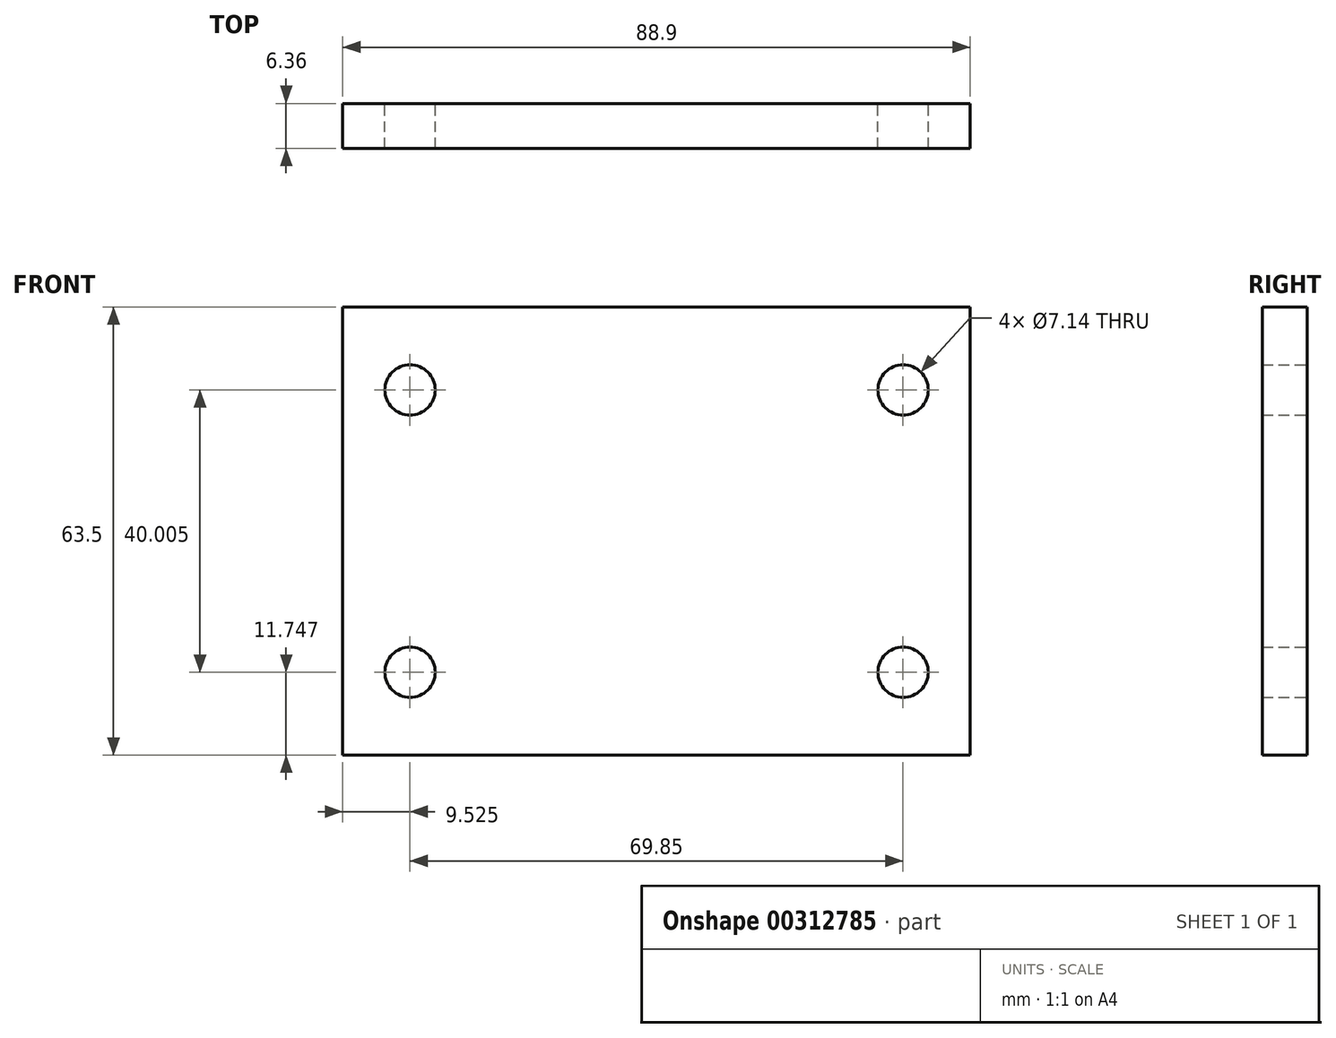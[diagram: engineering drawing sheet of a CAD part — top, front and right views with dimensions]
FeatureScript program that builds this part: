
annotation { "Feature Type Name" : "Feature", "Feature Type Description" : "" }
export const myFeature = defineFeature(function(context is Context, id is Id, definition is map)
    precondition{}
    {
        {
            var Q0;
            Q0=qCreatedBy(makeId("Front.planeOp"),FACE);
            var sketch = newSketch(context, id + "F0", { "sketchPlane" : qUnion([Q0])});
            skLineSegment(sketch, "E0.bottom", {"start": v(-44.45, 31.75) * mm, "end": v(44.45, 31.75) * mm});
            skLineSegment(sketch, "E0.top", {"start": v(-44.45, -31.75) * mm, "end": v(44.45, -31.75) * mm});
            skLineSegment(sketch, "E0.left", {"start": v(-44.45, 31.75) * mm, "end": v(-44.45, -31.75) * mm});
            skLineSegment(sketch, "E0.right", {"start": v(44.45, 31.75) * mm, "end": v(44.45, -31.75) * mm});
            skPoint(sketch, "E0.middle", {"position": v(0, 0) * mm});
            skCircle(sketch, "E1", {"center": v(-34.93, 20) * mm, "radius": 3.57 * mm});
            skCircle(sketch, "E2", {"center": v(-34.93, -20) * mm, "radius": 3.57 * mm});
            skCircle(sketch, "E3", {"center": v(34.93, -20) * mm, "radius": 3.57 * mm});
            skCircle(sketch, "E4", {"center": v(34.93, 20) * mm, "radius": 3.57 * mm});
            skLineSegment(sketch, "E5", {"start": v(0, 0) * mm, "end": v(0, 9.42) * mm});
            skLineSegment(sketch, "E6", {"start": v(0, 0) * mm, "end": v(10.27, 0) * mm});
            skSolve(sketch);
        }
        {
            var Q0;
            Q0 = qSketchRegion(id + "F0", true);
            extrude(context, id + "F1", {"entities" : qUnion([Q0]), "endBound" : BoundingType.SYMMETRIC, "depth" : 6.35 * mm});
        }
    });
